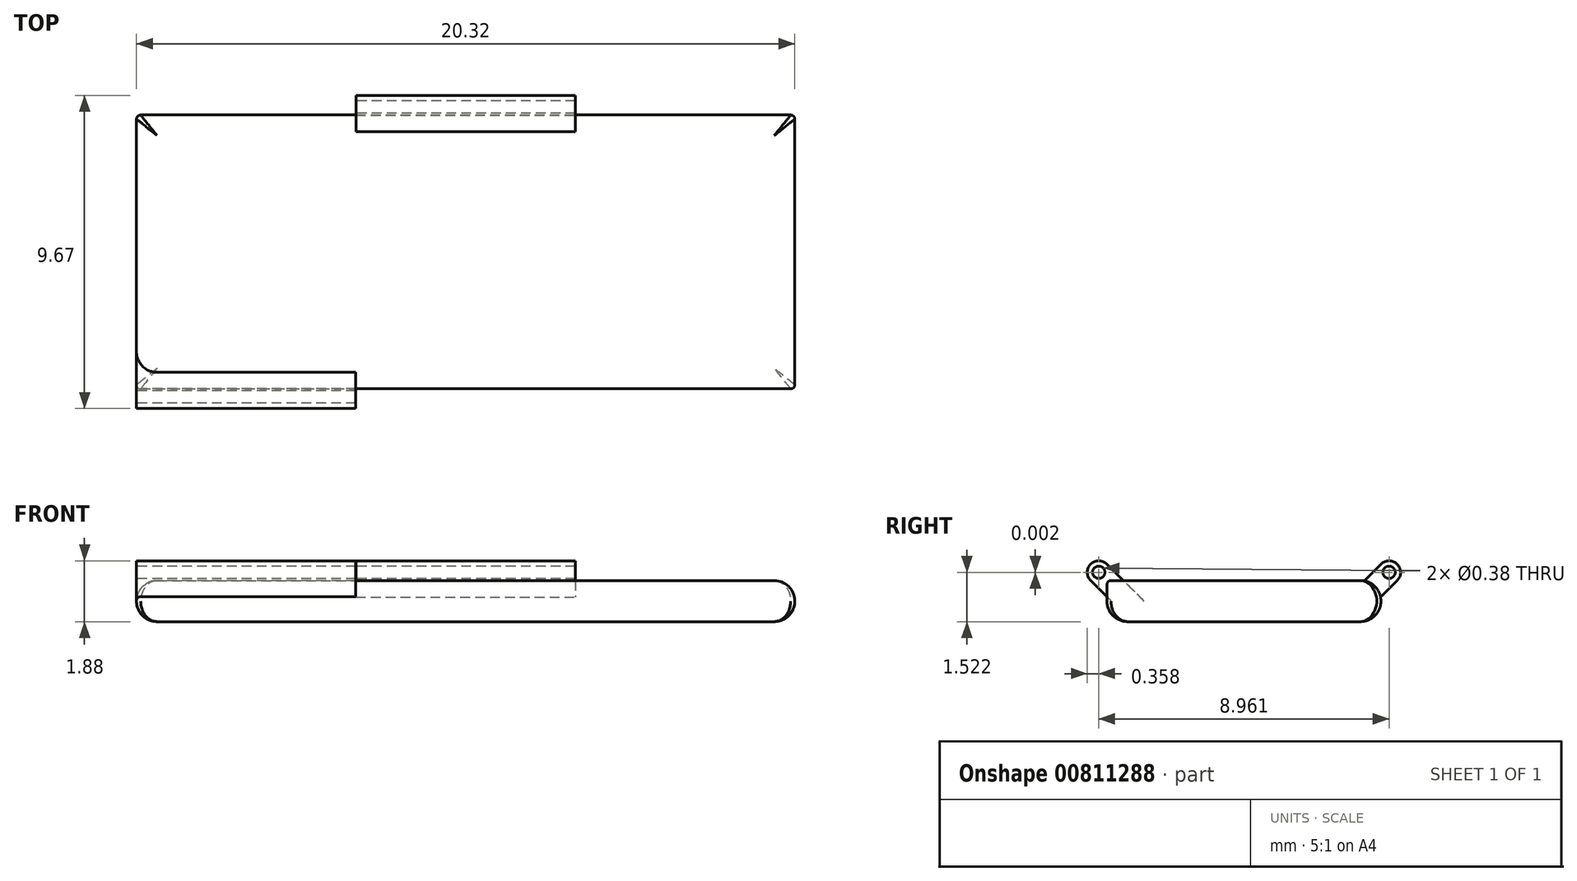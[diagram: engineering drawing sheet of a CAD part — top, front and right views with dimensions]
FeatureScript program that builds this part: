
annotation { "Feature Type Name" : "Feature", "Feature Type Description" : "" }
export const myFeature = defineFeature(function(context is Context, id is Id, definition is map)
    precondition{}
    {
        {
            var Q0;
            Q0=qCreatedBy(makeId("Top.planeOp"),FACE);
            var sketch = newSketch(context, id + "F0", { "sketchPlane" : qUnion([Q0])});
            skLineSegment(sketch, "E0.bottom", {"start": v(0, 0) * mm, "end": v(20.32, 0) * mm});
            skLineSegment(sketch, "E0.top", {"start": v(0, 8.46) * mm, "end": v(20.32, 8.46) * mm});
            skLineSegment(sketch, "E0.left", {"start": v(0, 0) * mm, "end": v(0, 8.46) * mm});
            skLineSegment(sketch, "E0.right", {"start": v(20.32, 0) * mm, "end": v(20.32, 8.46) * mm});
            skSolve(sketch);
        }
        {
            var Q0;
            Q0 = qSketchRegion(id + "F0", true);
            extrude(context, id + "F1", {"entities" : qUnion([Q0]), "depth" : 1.27 * mm, "offsetDistance" : 25.4 * mm});
        }
        {
            var Q0;
            Q0=qCreatedBy(makeId("Right.planeOp"),FACE);
            var sketch = newSketch(context, id + "F2", { "sketchPlane" : qUnion([Q0])});
            skLineSegment(sketch, "E1", {"start": v(0, 1.27) * mm, "end": v(-0.25, 1.52) * mm});
            skCircle(sketch, "E2", {"center": v(-0.25, 1.52) * mm, "radius": 0.36 * mm});
            skLineSegment(sketch, "E3.0", {"start": v(0, 1.27) * mm, "end": v(8.46, 1.27) * mm});
            skLineSegment(sketch, "E4.0", {"start": v(0, 1.27) * mm, "end": v(0, 0) * mm});
            skLineSegment(sketch, "E5", {"start": v(-0.25, 1.52) * mm, "end": v(-0.5, 1.27) * mm});
            skLineSegment(sketch, "E6", {"start": v(-0.25, 1.52) * mm, "end": v(0, 1.78) * mm});
            skLineSegment(sketch, "E7", {"start": v(0, 1.78) * mm, "end": v(0.5, 1.27) * mm});
            skLineSegment(sketch, "E8", {"start": v(-0.5, 1.27) * mm, "end": v(0, 0.77) * mm});
            skSolve(sketch);
        }
        {
            var Q0;
            Q0 = qSketchRegion(id + "F2", true);
            extrude(context, id + "F3", {"entities" : qUnion([Q0]), "operationType" : NewBodyOperationType.ADD, "depth" : 6.77 * mm, "offsetDistance" : 25.4 * mm});
        }
        {
            var Q0;
            Q0=makeQuery(id+"F3.boolean.opBoolean","MERGE",FACE,{"derivedFrom":[makeQuery(id+"F1.opExtrude","SWEPT_FACE",FACE,{"disambiguationData":[OSD([sQuery(id+"F0.wireOp",EDGE,"E0.left")])]}),makeQuery(id+"F3.opExtrude","CAP_FACE",FACE,{"disambiguationData":[OSD([sQuery(id+"F2.wireOp",EDGE,"E2"),sQuery(id+"F2.wireOp",EDGE,"E3.0"),sQuery(id+"F2.wireOp",EDGE,"E4.0"),sQuery(id+"F2.wireOp",EDGE,"E7"),sQuery(id+"F2.wireOp",EDGE,"E8")])],"isStart":true})]});
            cPlane(context, id + "F4", {"entities" : qUnion([Q0]), "cplaneType" : CPlaneType.OFFSET, "offset" : 10.16 * mm, "oppositeDirection" : true, "width" : 152.4 * mm, "height" : 152.4 * mm});
        }
        {
            var Q0;
            Q0=qCreatedBy(id+"F4.planeOp",FACE);
            var sketch = newSketch(context, id + "F5", { "sketchPlane" : qUnion([Q0])});
            skLineSegment(sketch, "E9.0", {"start": v(-0.5, 1.27) * mm, "end": v(-8.46, 1.27) * mm});
            skLineSegment(sketch, "E10.0", {"start": v(-8.46, 1.27) * mm, "end": v(-8.46, 0) * mm});
            skLineSegment(sketch, "E11", {"start": v(-8.46, 1.27) * mm, "end": v(-8.7, 1.52) * mm});
            skCircle(sketch, "E12", {"center": v(-8.7, 1.52) * mm, "radius": 0.36 * mm});
            skLineSegment(sketch, "E13", {"start": v(-8.7, 1.52) * mm, "end": v(-8.46, 1.77) * mm});
            skLineSegment(sketch, "E14", {"start": v(-8.46, 1.77) * mm, "end": v(-7.96, 1.27) * mm});
            skLineSegment(sketch, "E15", {"start": v(-8.7, 1.52) * mm, "end": v(-8.96, 1.27) * mm});
            skLineSegment(sketch, "E16", {"start": v(-8.96, 1.27) * mm, "end": v(-8.46, 0.77) * mm});
            skSolve(sketch);
        }
        {
            var Q0;
            Q0 = qSketchRegion(id + "F5", true);
            extrude(context, id + "F6", {"entities" : qUnion([Q0]), "operationType" : NewBodyOperationType.ADD, "depth" : 3.4 * mm, "offsetDistance" : 25.4 * mm, "hasSecondDirection" : true, "secondDirectionOppositeDirection" : true, "secondDirectionDepth" : 3.4 * mm});
        }
        {
            var Q0;
            Q0=makeQuery(id+"F6.opExtrude","CAP_FACE",FACE,{"disambiguationData":[OSD([sQuery(id+"F5.wireOp",EDGE,"E9.0"),sQuery(id+"F5.wireOp",EDGE,"E10.0"),sQuery(id+"F5.wireOp",EDGE,"E12"),sQuery(id+"F5.wireOp",EDGE,"E14"),sQuery(id+"F5.wireOp",EDGE,"E16")])],"isStart":false});
            var sketch = newSketch(context, id + "F7", { "sketchPlane" : qUnion([Q0])});
            skCircle(sketch, "E17", {"center": v(-8.7, 1.52) * mm, "radius": 0.2 * mm});
            skArc(sketch, "E18.0", {"start": v(0, 1.78) * mm, "mid": v(0.5, 1.78) * mm, "end": v(0.5, 1.27) * mm});
            skCircle(sketch, "E19", {"center": v(0.25, 1.52) * mm, "radius": 0.2 * mm});
            skSolve(sketch);
        }
        {
            var Q0;
            Q0 = qSketchRegion(id + "F7", true);
            extrude(context, id + "F8", {"entities" : qUnion([Q0]), "operationType" : NewBodyOperationType.REMOVE, "oppositeDirection" : true, "depth" : 25.4 * mm, "offsetDistance" : 25.4 * mm, "hasSecondDirection" : true, "secondDirectionOppositeDirection" : false, "secondDirectionDepth" : 25.4 * mm});
        }
        {
            var Q0;
            Q0=makeQuery(id+"F1.opExtrude","CAP_EDGE",EDGE,{"disambiguationData":[OSD([sQuery(id+"F0.wireOp",EDGE,"E0.bottom")])],"isStart":true});
            var Q1;
            Q1=makeQuery(id+"F1.opExtrude","CAP_EDGE",EDGE,{"disambiguationData":[OSD([sQuery(id+"F0.wireOp",EDGE,"E0.top")])],"isStart":true});
            var Q2;
            {var subQ0=sQuery(id+"F0.wireOp",EDGE,"E0.left");var subQ1=sQuery(id+"F0.wireOp",EDGE,"E0.top");Q2=makeQuery(id+"F6.boolean.opBoolean","SPLIT",EDGE,{"disambiguationData":[TD([makeQuery(id+"F1.opExtrude","SWEPT_FACE",FACE,{"disambiguationData":[OSD([subQ0])]})])],"derivedFrom":makeQuery(id+"F1.opExtrude","CAP_EDGE",EDGE,{"disambiguationData":[OSD([subQ1])],"isStart":false})});}
            var Q3;
            Q3=makeQuery(id+"F1.opExtrude","CAP_EDGE",EDGE,{"disambiguationData":[OSD([sQuery(id+"F0.wireOp",EDGE,"E0.left")])],"isStart":false});
            var Q4;
            Q4=makeQuery(id+"F1.opExtrude","CAP_EDGE",EDGE,{"disambiguationData":[OSD([sQuery(id+"F0.wireOp",EDGE,"E0.left")])],"isStart":true});
            var Q5;
            Q5=makeQuery(id+"F1.opExtrude","CAP_EDGE",EDGE,{"disambiguationData":[OSD([sQuery(id+"F0.wireOp",EDGE,"E0.right")])],"isStart":false});
            var Q6;
            Q6=makeQuery(id+"F1.opExtrude","CAP_EDGE",EDGE,{"disambiguationData":[OSD([sQuery(id+"F0.wireOp",EDGE,"E0.right")])],"isStart":true});
            fillet(context, id + "F9", {"entities" : qUnion([Q0, Q1, Q2, Q3, Q4, Q5, Q6]), "radius" : 0.64 * mm, "tangentPropagation" : true, "allowEdgeOverflow" : false});
        }
        {
            var Q0;
            Q0=makeQuery(id+"F9.opFillet","BLEND_EDGE",EDGE,{"blendedFrom":[makeQuery(id+"F1.opExtrude","CAP_EDGE",EDGE,{"disambiguationData":[OSD([sQuery(id+"F0.wireOp",EDGE,"E0.bottom")])],"isStart":true}),makeQuery(id+"F1.opExtrude","CAP_EDGE",EDGE,{"disambiguationData":[OSD([sQuery(id+"F0.wireOp",EDGE,"E0.left")])],"isStart":true})],"blendedInto":[]});
            var Q1;
            Q1=makeQuery(id+"F9.opFillet","BLEND_EDGE",EDGE,{"blendedFrom":[makeQuery(id+"F1.opExtrude","CAP_EDGE",EDGE,{"disambiguationData":[OSD([sQuery(id+"F0.wireOp",EDGE,"E0.bottom")])],"isStart":true}),makeQuery(id+"F1.opExtrude","CAP_EDGE",EDGE,{"disambiguationData":[OSD([sQuery(id+"F0.wireOp",EDGE,"E0.right")])],"isStart":true})],"blendedInto":[]});
            var Q2;
            Q2=makeQuery(id+"F9.opFillet","BLEND_EDGE",EDGE,{"blendedFrom":[makeQuery(id+"F1.opExtrude","CAP_EDGE",EDGE,{"disambiguationData":[OSD([sQuery(id+"F0.wireOp",EDGE,"E0.top")])],"isStart":true}),makeQuery(id+"F1.opExtrude","CAP_EDGE",EDGE,{"disambiguationData":[OSD([sQuery(id+"F0.wireOp",EDGE,"E0.right")])],"isStart":true})],"blendedInto":[]});
            var Q3;
            Q3=makeQuery(id+"F9.opFillet","BLEND_EDGE",EDGE,{"blendedFrom":[makeQuery(id+"F1.opExtrude","CAP_EDGE",EDGE,{"disambiguationData":[OSD([sQuery(id+"F0.wireOp",EDGE,"E0.top")])],"isStart":true}),makeQuery(id+"F1.opExtrude","CAP_EDGE",EDGE,{"disambiguationData":[OSD([sQuery(id+"F0.wireOp",EDGE,"E0.left")])],"isStart":true})],"blendedInto":[]});
            fillet(context, id + "F10", {"entities" : qUnion([Q0, Q1, Q2, Q3]), "radius" : 0.13 * mm, "tangentPropagation" : true, "allowEdgeOverflow" : false});
        }
    });
